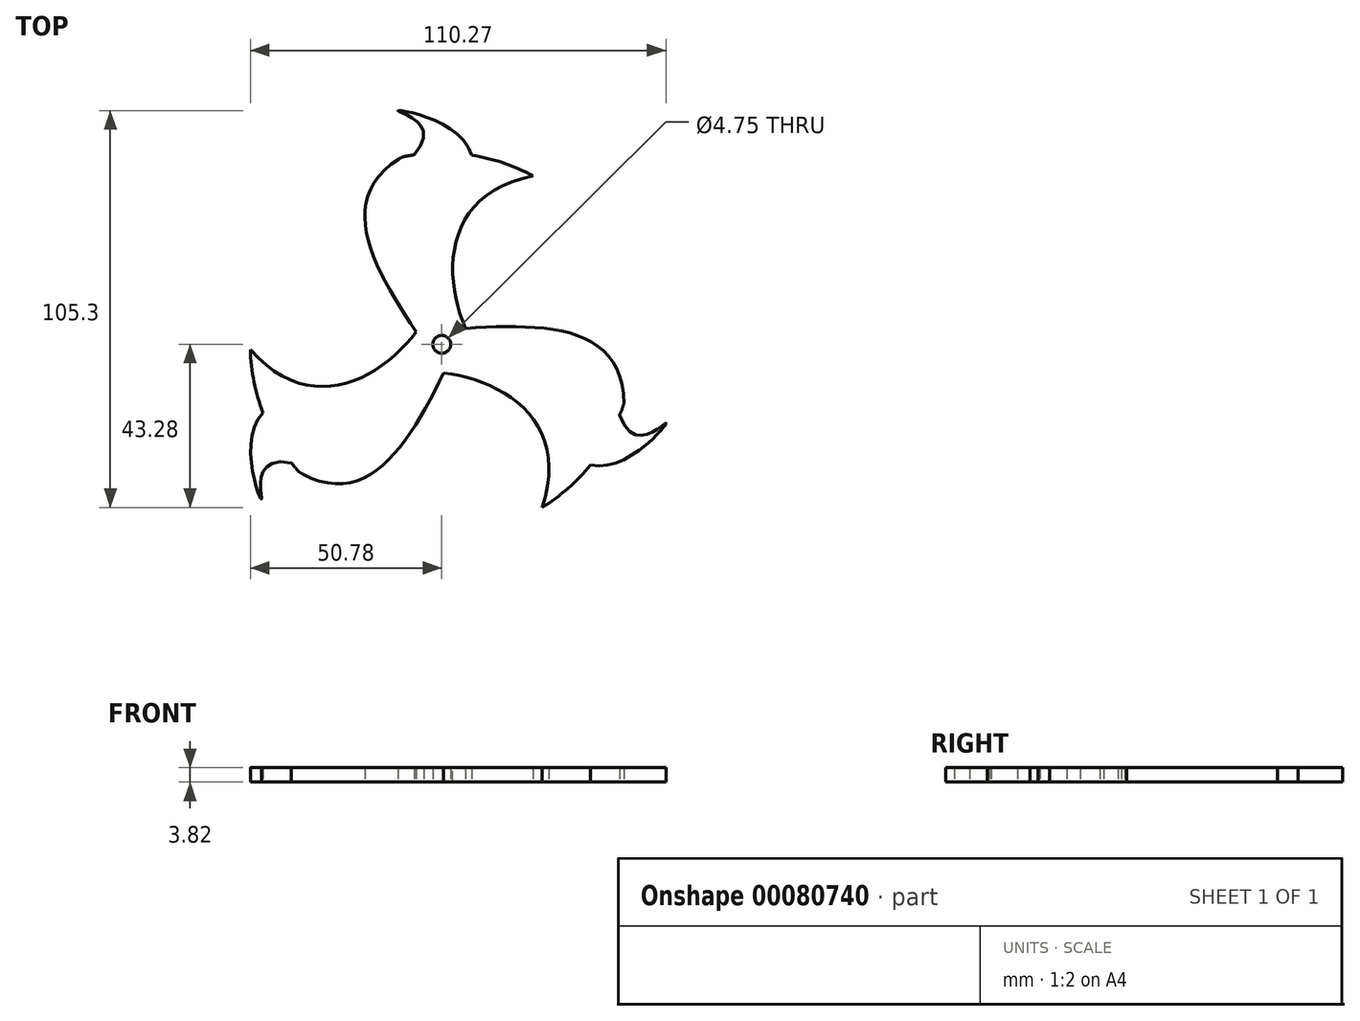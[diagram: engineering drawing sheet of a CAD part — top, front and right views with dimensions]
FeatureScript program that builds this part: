
annotation { "Feature Type Name" : "Feature", "Feature Type Description" : "" }
export const myFeature = defineFeature(function(context is Context, id is Id, definition is map)
    precondition{}
    {
        {
            var Q0;
            Q0=qCreatedBy(makeId("Top.planeOp"),FACE);
            var sketch = newSketch(context, id + "F0", { "sketchPlane" : qUnion([Q0])});
            skCircle(sketch, "E0", {"center": v(0, 0) * mm, "radius": 50.8 * mm});
            skCircle(sketch, "E1", {"center": v(0, 0) * mm, "radius": 2.37 * mm});
            skCircle(sketch, "E2", {"center": v(0, 0) * mm, "radius": 7.5 * mm});
            skFitSpline(sketch, "E3", {"points": [v(-6.76, 3.23) * mm, v(-10.56, 49.69) * mm], "startDerivative": vector(-34.7, 51.98) * mm, "endDerivative": vector(54.42, 32.42) * mm});
            skFitSpline(sketch, "E4", {"points": [v(6.8, 3.16) * mm, v(24.18, 44.68) * mm], "startDerivative": vector(-20.38, 43.44) * mm, "endDerivative": vector(72.54, 14.32) * mm});
            skFitSpline(sketch, "E5", {"points": [v(7.93, 50.18) * mm, v(-11.6, 61.89) * mm, v(-7.28, 50.28) * mm], "startDerivative": vector(-14.05, 50.07) * mm, "endDerivative": vector(-51.46, -59.06) * mm});
            skSolve(sketch);
        }
        {
            var Q0;
            {var subQ0=sQuery(id+"F0.wireOp",EDGE,"E3");Q0=makeQuery(id+"F0.imprint","IMPRINT",FACE,{"disambiguationData":[TD([[makeQuery(id+"F0.imprint","IMPRINT",EDGE,{"derivedFrom":subQ0}),-1.0]])]});}
            var Q1;
            Q1=makeQuery(id+"F0.imprint","IMPRINT",FACE,{"disambiguationData":[TD([[makeQuery(id+"F0.imprint","IMPRINT",EDGE,{"derivedFrom":sQuery(id+"F0.wireOp",EDGE,"E1")}),-1.0]])]});
            var Q2;
            {var subQ0=sQuery(id+"F0.wireOp",EDGE,"E5");Q2=makeQuery(id+"F0.imprint","IMPRINT",FACE,{"disambiguationData":[TD([[makeQuery(id+"F0.imprint","IMPRINT",EDGE,{"derivedFrom":subQ0}),1.0]])]});}
            extrude(context, id + "F1", {"entities" : qUnion([Q0, Q1, Q2]), "endBound" : BoundingType.SYMMETRIC, "depth" : 3.8 * mm});
        }
        {
            var Q0;
            Q0=makeQuery(id+"F1.opExtrude","SWEPT_BODY",BODY,{"disambiguationData":[OSD([sQuery(id+"F0.wireOp",EDGE,"E0"),sQuery(id+"F0.wireOp",EDGE,"E1"),sQuery(id+"F0.wireOp",EDGE,"E2"),sQuery(id+"F0.wireOp",EDGE,"E3"),sQuery(id+"F0.wireOp",EDGE,"E4"),sQuery(id+"F0.wireOp",EDGE,"E5")])]});
            var Q1;
            Q1=makeQuery(id+"F1.opExtrude","CAP_EDGE",EDGE,{"disambiguationData":[OSD([sQuery(id+"F0.wireOp",EDGE,"E1")])],"isStart":false});
            circularPattern(context, id + "F2", {"operationType" : NewBodyOperationType.ADD, "entities" : qUnion([Q0]), "axis" : qUnion([Q1]), "angle" : 360 * degree, "instanceCount" : 3, "equalSpace" : true});
        }
        {
            var Q0;
            Q0=makeQuery(id+"F1.opExtrude","SWEPT_EDGE",EDGE,{"disambiguationData":[OSD([sQuery(id+"F0.wireOp",EDGE,"E0"),sQuery(id+"F0.wireOp",EDGE,"E3")])]});
            var Q1;
            Q1=makeQuery(id+"F2.opPattern","COPY",EDGE,{"derivedFrom":makeQuery(id+"F1.opExtrude","SWEPT_EDGE",EDGE,{"disambiguationData":[OSD([sQuery(id+"F0.wireOp",EDGE,"E0"),sQuery(id+"F0.wireOp",EDGE,"E3")])]}),"instanceName":"1"});
            fillet(context, id + "F3", {"entities" : qUnion([Q0, Q1]), "radius" : 5.08 * mm, "tangentPropagation" : true, "allowEdgeOverflow" : false});
        }
    });
